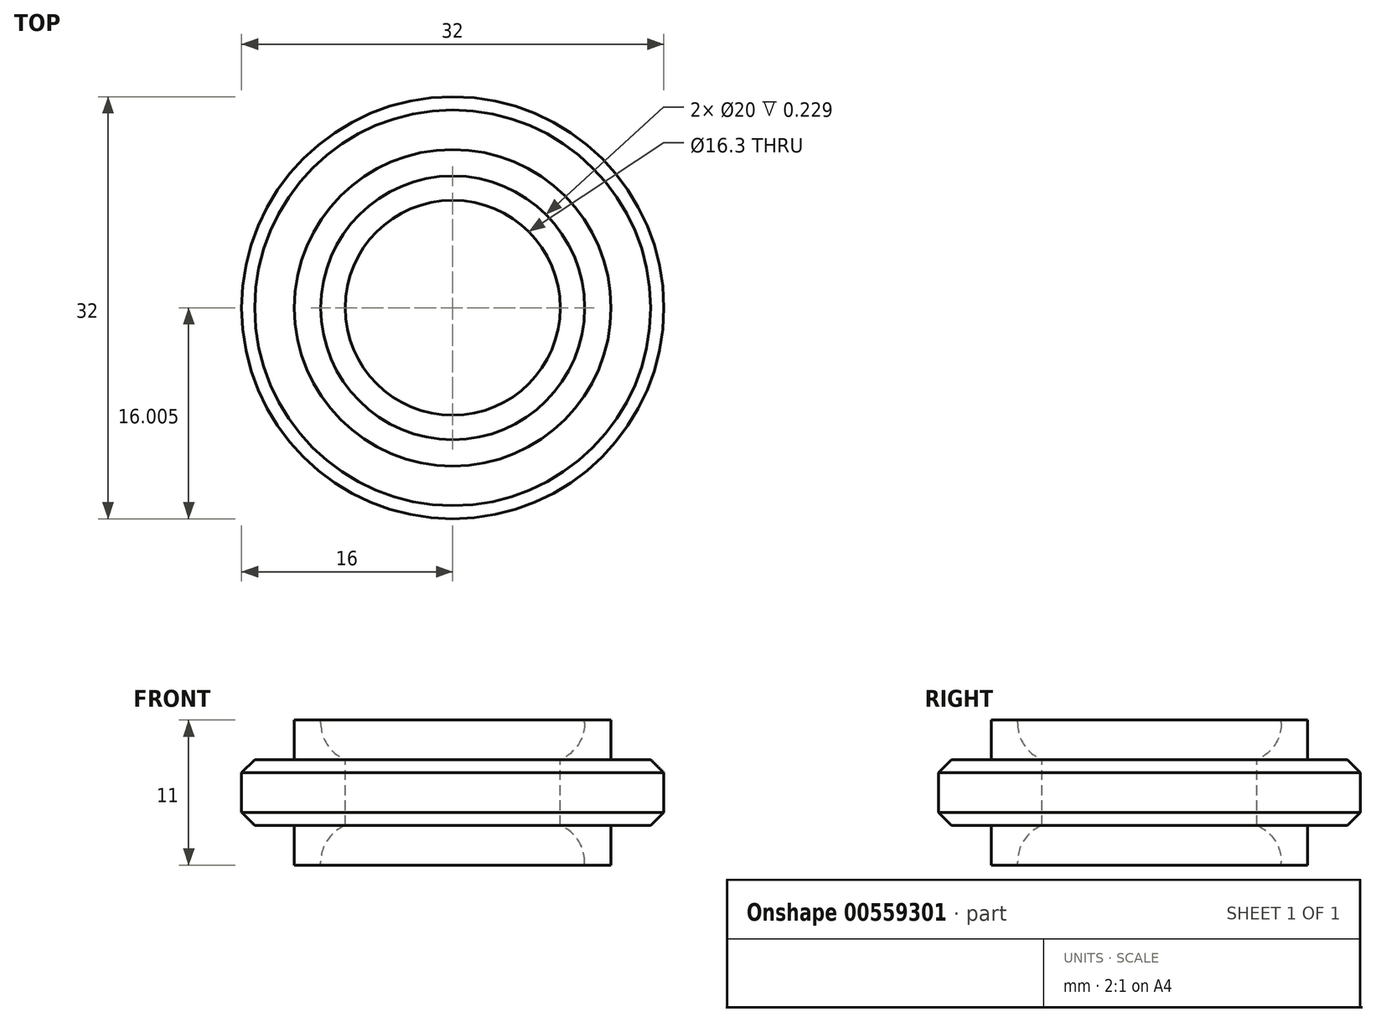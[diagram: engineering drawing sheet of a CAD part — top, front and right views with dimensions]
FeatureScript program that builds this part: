
annotation { "Feature Type Name" : "Feature", "Feature Type Description" : "" }
export const myFeature = defineFeature(function(context is Context, id is Id, definition is map)
    precondition{}
    {
        {
            var Q0;
            Q0=qCreatedBy(makeId("Right.planeOp"),FACE);
            var sketch = newSketch(context, id + "F0", { "sketchPlane" : qUnion([Q0])});
            skLineSegment(sketch, "E0.bottom", {"start": v(-7.45, 4.42) * mm, "end": v(0.7, 4.42) * mm});
            skLineSegment(sketch, "E0.top", {"start": v(-7.45, -0.58) * mm, "end": v(0.7, -0.58) * mm});
            skLineSegment(sketch, "E0.left", {"start": v(-7.45, 4.42) * mm, "end": v(-7.45, -0.58) * mm});
            skLineSegment(sketch, "E0.right", {"start": v(0.7, 4.42) * mm, "end": v(0.7, -0.58) * mm});
            skLineSegment(sketch, "E1", {"start": v(0.7, 4.42) * mm, "end": v(2.55, 4.42) * mm});
            skLineSegment(sketch, "E2", {"start": v(2.55, 4.42) * mm, "end": v(2.55, -0.58) * mm});
            skLineSegment(sketch, "E3", {"start": v(2.55, -0.58) * mm, "end": v(0.7, -0.58) * mm});
            skLineSegment(sketch, "E4", {"start": v(2.55, 4.42) * mm, "end": v(2.55, 7.42) * mm});
            skLineSegment(sketch, "E5", {"start": v(2.55, 7.42) * mm, "end": v(4.55, 7.42) * mm});
            skLineSegment(sketch, "E6", {"start": v(4.55, 7.42) * mm, "end": v(4.55, 4.42) * mm});
            skLineSegment(sketch, "E7", {"start": v(4.55, 4.42) * mm, "end": v(8.55, 4.42) * mm});
            skLineSegment(sketch, "E8", {"start": v(8.55, 4.42) * mm, "end": v(8.55, -0.58) * mm});
            skLineSegment(sketch, "E9", {"start": v(8.55, -0.58) * mm, "end": v(4.55, -0.58) * mm});
            skLineSegment(sketch, "E10", {"start": v(4.55, -0.58) * mm, "end": v(4.55, -3.58) * mm});
            skLineSegment(sketch, "E11", {"start": v(4.55, -3.58) * mm, "end": v(2.55, -3.58) * mm});
            skLineSegment(sketch, "E12", {"start": v(2.55, -3.58) * mm, "end": v(2.55, -0.58) * mm});
            skSolve(sketch);
        }
        {
            var Q0;
            Q0=makeQuery(id+"F0.imprint","IMPRINT",FACE,{"disambiguationData":[TD([[makeQuery(id+"F0.imprint","IMPRINT",EDGE,{"derivedFrom":sQuery(id+"F0.wireOp",EDGE,"E0.right")}),1.0]])]});
            var Q1;
            Q1=makeQuery(id+"F0.imprint","IMPRINT",FACE,{"disambiguationData":[TD([[makeQuery(id+"F0.imprint","IMPRINT",EDGE,{"derivedFrom":sQuery(id+"F0.wireOp",EDGE,"E2")}),1.0]])]});
            var Q2;
            Q2=sQuery(id+"F0.wireOp",EDGE,"E0.left");
            revolve(context, id + "F1", {"surfaceOperationType" : NewSurfaceOperationType.NEW, "entities" : qUnion([Q0, Q1]), "axis" : qUnion([Q2]), "revolveType" : RevolveType.FULL});
        }
        {
            var Q0;
            Q0=makeQuery(id+"F1.opRevolve","SWEPT_EDGE",EDGE,{"disambiguationData":[OSD([sQuery(id+"F0.wireOp",EDGE,"E1"),sQuery(id+"F0.wireOp",EDGE,"E2"),sQuery(id+"F0.wireOp",EDGE,"E4")])]});
            var Q1;
            Q1=makeQuery(id+"F1.opRevolve","SWEPT_EDGE",EDGE,{"disambiguationData":[OSD([sQuery(id+"F0.wireOp",EDGE,"E2"),sQuery(id+"F0.wireOp",EDGE,"E3"),sQuery(id+"F0.wireOp",EDGE,"E12")])]});
            fillet(context, id + "F2", {"entities" : qUnion([Q0, Q1]), "tangentPropagation" : true, "radius" : 3 * mm, "defaultsChanged" : false, "vertexSettings" : [], "allowEdgeOverflow" : false});
        }
        {
            var Q0;
            Q0=makeQuery(id+"F1.opRevolve","SWEPT_EDGE",EDGE,{"disambiguationData":[OSD([sQuery(id+"F0.wireOp",EDGE,"E8"),sQuery(id+"F0.wireOp",EDGE,"E9")])]});
            var Q1;
            Q1=makeQuery(id+"F1.opRevolve","SWEPT_EDGE",EDGE,{"disambiguationData":[OSD([sQuery(id+"F0.wireOp",EDGE,"E7"),sQuery(id+"F0.wireOp",EDGE,"E8")])]});
            chamfer(context, id + "F3", {"entities" : qUnion([Q0, Q1]), "width" : 1 * mm, "tangentPropagation" : true});
        }
    });
